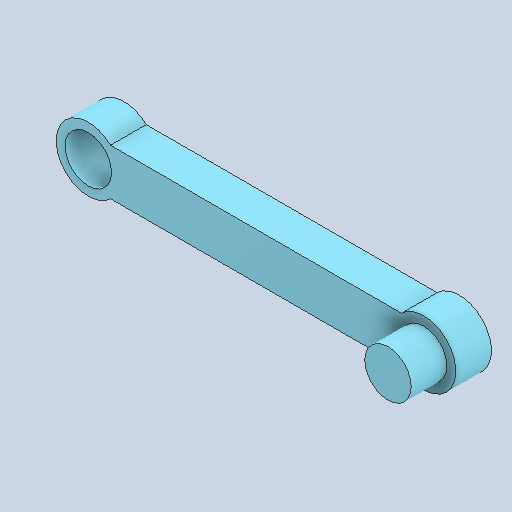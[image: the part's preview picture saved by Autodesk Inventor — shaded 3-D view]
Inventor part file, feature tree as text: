
AUTODESK INVENTOR PART (.ipt)
format: ipt  version: 2022 (Build 260153000, 153)  size: 111,104 bytes
history: native  units: in
note: dims shown in document units (in); Inventor stores cm internally (conversion verified against a paired STEP export)
features: other x3, sketch x1
ambient origin geometry x8: Origin, YZ Plane, XZ Plane, XY Plane, X Axis, Y Axis, Z Axis, Center Point
bodies: Solid1 (feature_tree)
feature tree (4):
  other  "Component39.ipt"
  other  "Solid1::Component39.ipt"
  other  "TaggingFeature1"
  sketch  "Sketch2"  dims[d0=0.3937in]
